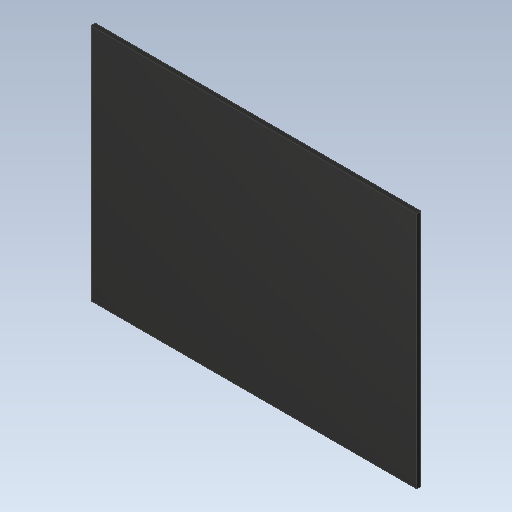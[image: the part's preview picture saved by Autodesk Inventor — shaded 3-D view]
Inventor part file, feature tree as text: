
AUTODESK INVENTOR PART (.ipt)
format: ipt  version: 2020 (Build 240168000, 168)  size: 87,040 bytes
history: imported  units: in
note: dims shown in document units (in); Inventor stores cm internally (conversion verified against a paired STEP export)
features: imported_body x1
ambient origin geometry x8: Origin, YZ Plane, XZ Plane, XY Plane, X Axis, Y Axis, Z Axis, Center Point
bodies: Solid1 (imported_parasolid), Body1 (imported_parasolid)
feature tree (1):
  imported_body  NMx_Import_Brep_tag  [imported B-rep: ~6 faces, bbox_mm=[7.45, 5.45, 0.1]]
